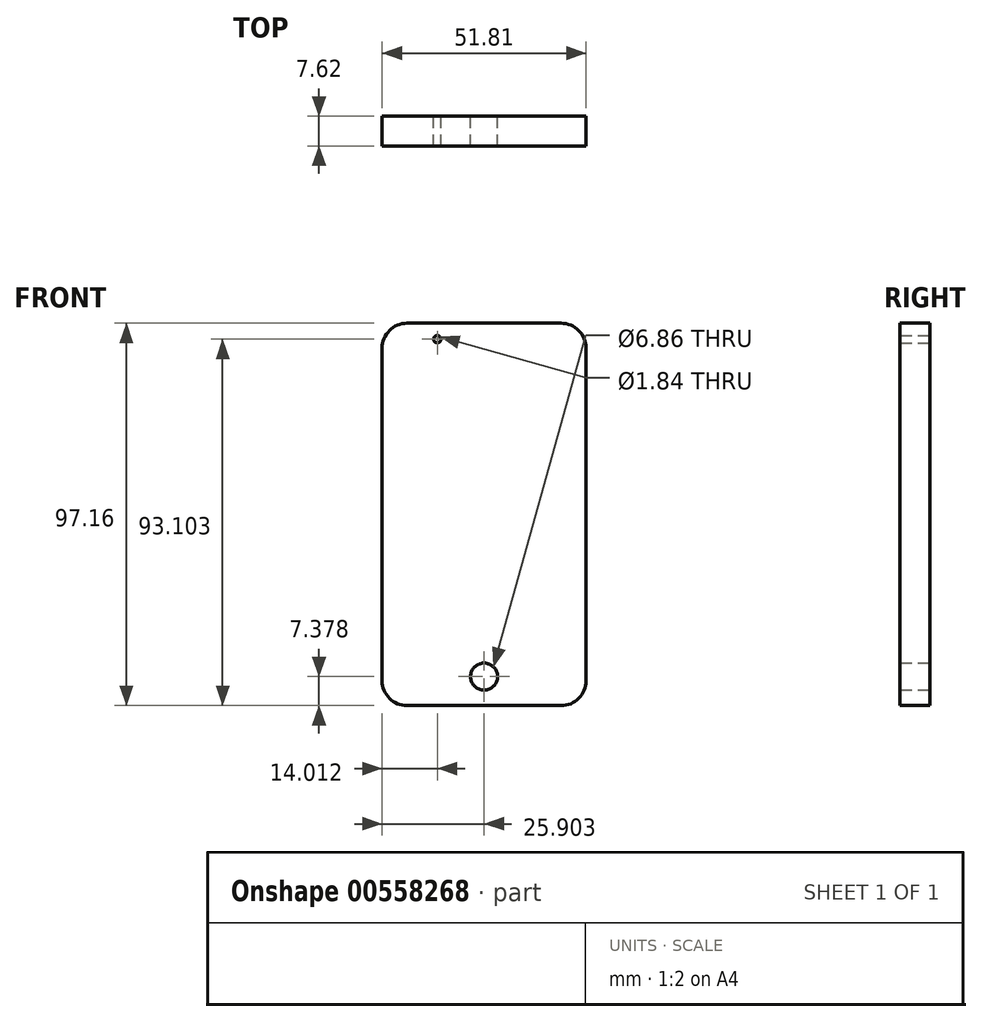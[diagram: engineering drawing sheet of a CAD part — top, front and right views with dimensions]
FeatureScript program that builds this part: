
annotation { "Feature Type Name" : "Feature", "Feature Type Description" : "" }
export const myFeature = defineFeature(function(context is Context, id is Id, definition is map)
    precondition{}
    {
        {
            var Q0;
            Q0=qCreatedBy(makeId("Front.planeOp"),FACE);
            var sketch = newSketch(context, id + "F0", { "sketchPlane" : qUnion([Q0])});
            skLineSegment(sketch, "E0", {"start": v(-34.66, 39.74) * mm, "end": v(-34.66, -44.72) * mm});
            skLineSegment(sketch, "E1", {"start": v(-28.3, 46.09) * mm, "end": v(10.8, 46.09) * mm});
            skLineSegment(sketch, "E2", {"start": v(17.15, 39.74) * mm, "end": v(17.15, -44.72) * mm});
            skLineSegment(sketch, "E3", {"start": v(-28.3, -51.07) * mm, "end": v(10.8, -51.07) * mm});
            skPoint(sketch, "E4.visualSharp", {"position": v(-34.66, 46.09) * mm});
            skArc(sketch, "E4.filletArc", {"start": v(-28.3, 46.09) * mm, "mid": v(-32.8, 44.23) * mm, "end": v(-34.66, 39.74) * mm});
            skPoint(sketch, "E5.visualSharp", {"position": v(17.15, 46.09) * mm});
            skArc(sketch, "E5.filletArc", {"start": v(17.15, 39.74) * mm, "mid": v(15.29, 44.23) * mm, "end": v(10.8, 46.09) * mm});
            skPoint(sketch, "E6.visualSharp", {"position": v(17.15, -51.07) * mm});
            skArc(sketch, "E6.filletArc", {"start": v(10.8, -51.07) * mm, "mid": v(15.29, -49.2) * mm, "end": v(17.15, -44.72) * mm});
            skPoint(sketch, "E7.visualSharp", {"position": v(-34.66, -51.07) * mm});
            skArc(sketch, "E7.filletArc", {"start": v(-34.66, -44.72) * mm, "mid": v(-32.8, -49.2) * mm, "end": v(-28.3, -51.07) * mm});
            skLineSegment(sketch, "E8", {"start": v(-34.66, 36.32) * mm, "end": v(17.15, 36.32) * mm});
            skLineSegment(sketch, "E9", {"start": v(-34.66, -38.71) * mm, "end": v(17.15, -38.71) * mm});
            skCircle(sketch, "E10", {"center": v(-8.76, -43.7) * mm, "radius": 3.43 * mm});
            skPoint(sketch, "E10.centerSnap0", {"position": v(-8.76, -38.71) * mm});
            skCircle(sketch, "E11", {"center": v(-20.65, 42.03) * mm, "radius": 0.92 * mm});
            skLineSegment(sketch, "E12", {"start": v(-13.46, 41.66) * mm, "end": v(-2.77, 41.66) * mm});
            skSolve(sketch);
        }
        {
            var Q0;
            Q0 = qSketchRegion(id + "F0", true);
            extrude(context, id + "F1", {"entities" : qUnion([Q0]), "depth" : 1.27 * mm, "offsetDistance" : 25.4 * mm});
        }
        {
            var Q0;
            Q0 = qSketchRegion(id + "F0", true);
            extrude(context, id + "F2", {"entities" : qUnion([Q0]), "operationType" : NewBodyOperationType.ADD, "depth" : 7.62 * mm, "offsetDistance" : 25.4 * mm});
        }
    });
